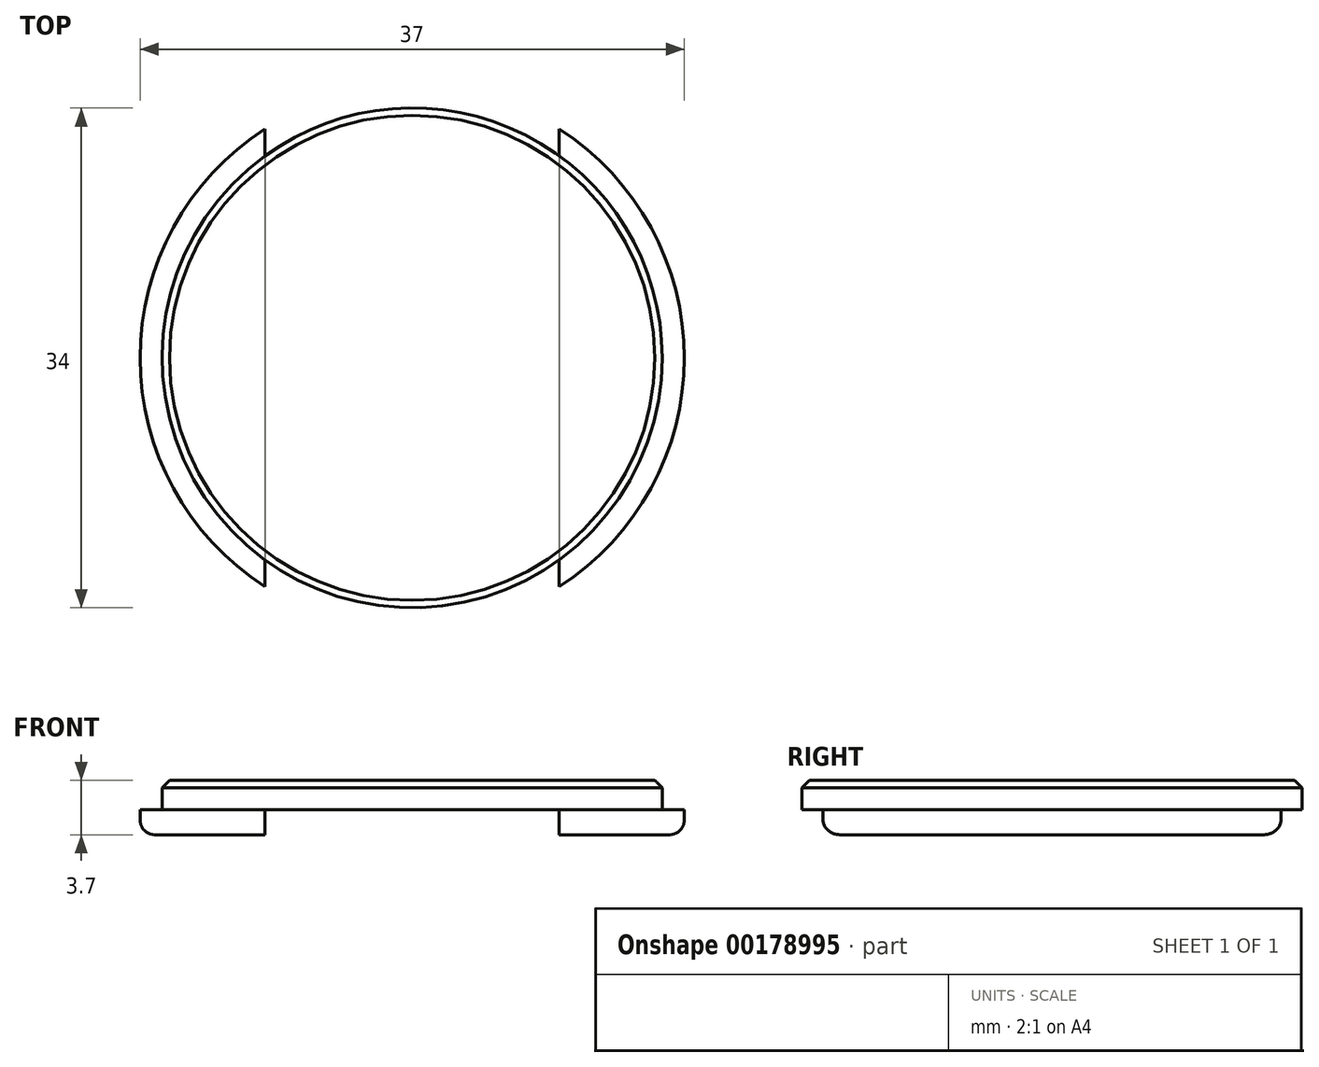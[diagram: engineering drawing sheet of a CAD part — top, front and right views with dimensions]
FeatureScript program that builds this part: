
annotation { "Feature Type Name" : "Feature", "Feature Type Description" : "" }
export const myFeature = defineFeature(function(context is Context, id is Id, definition is map)
    precondition{}
    {
        {
            var Q0;
            Q0=qCreatedBy(makeId("Top.planeOp"),FACE);
            var sketch = newSketch(context, id + "F0", { "sketchPlane" : qUnion([Q0])});
            skCircle(sketch, "E0", {"center": v(0, 0) * mm, "radius": 18.5 * mm});
            skSolve(sketch);
        }
        {
            var Q0;
            Q0 = qSketchRegion(id + "F0", true);
            extrude(context, id + "F1", {"entities" : qUnion([Q0]), "depth" : 1.7 * mm});
        }
        {
            var Q0;
            Q0=makeQuery(id+"F1.opExtrude","CAP_FACE",FACE,{"disambiguationData":[OSD([sQuery(id+"F0.wireOp",EDGE,"E0")])],"isStart":false});
            var sketch = newSketch(context, id + "F2", { "sketchPlane" : qUnion([Q0])});
            skCircle(sketch, "E1", {"center": v(0, 0) * mm, "radius": 17 * mm});
            skSolve(sketch);
        }
        {
            var Q0;
            Q0 = qSketchRegion(id + "F2", true);
            extrude(context, id + "F3", {"entities" : qUnion([Q0]), "operationType" : NewBodyOperationType.ADD, "depth" : 2 * mm});
        }
        {
            var Q0;
            Q0=makeQuery(id+"F3.opExtrude","CAP_EDGE",EDGE,{"disambiguationData":[OSD([sQuery(id+"F2.wireOp",EDGE,"E1")])],"isStart":false});
            chamfer(context, id + "F4", {"entities" : qUnion([Q0]), "width" : .5 * mm, "tangentPropagation" : true});
        }
        {
            var Q0;
            Q0=makeQuery(id+"F1.opExtrude","CAP_FACE",FACE,{"disambiguationData":[OSD([sQuery(id+"F0.wireOp",EDGE,"E0")])],"isStart":true});
            fillet(context, id + "F5", {"entities" : qUnion([Q0]), "radius" : 1 * mm, "tangentPropagation" : true, "allowEdgeOverflow" : false});
        }
        {
            var Q0;
            Q0=makeQuery(id+"F1.opExtrude","CAP_FACE",FACE,{"disambiguationData":[OSD([sQuery(id+"F0.wireOp",EDGE,"E0")])],"isStart":true});
            var sketch = newSketch(context, id + "F6", { "sketchPlane" : qUnion([Q0])});
            skLineSegment(sketch, "E2.bottom", {"start": v(10, -27.67) * mm, "end": v(-10, -27.67) * mm});
            skLineSegment(sketch, "E2.top", {"start": v(10, 27.67) * mm, "end": v(-10, 27.67) * mm});
            skLineSegment(sketch, "E2.left", {"start": v(10, -27.67) * mm, "end": v(10, 27.67) * mm});
            skLineSegment(sketch, "E2.right", {"start": v(-10, -27.67) * mm, "end": v(-10, 27.67) * mm});
            skPoint(sketch, "E2.middle", {"position": v(0, 0) * mm});
            skSolve(sketch);
        }
        {
            var Q0;
            Q0 = qSketchRegion(id + "F6", true);
            extrude(context, id + "F7", {"entities" : qUnion([Q0]), "operationType" : NewBodyOperationType.REMOVE, "oppositeDirection" : true, "depth" : 1.7 * mm});
        }
    });
